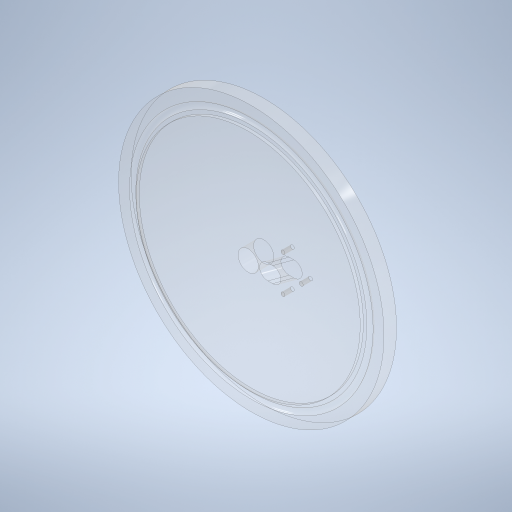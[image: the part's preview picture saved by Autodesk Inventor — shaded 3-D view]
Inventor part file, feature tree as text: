
AUTODESK INVENTOR PART (.ipt)
format: ipt  version: 2023.1 (Build 271208000, 208)  size: 331,264 bytes
history: native  units: mm
features: sketch x7, extrude x4, plane x1, hole x1, revolve x1, other x1
ambient origin geometry x8: Origin, YZ Plane, XZ Plane, XY Plane, X Axis, Y Axis, Z Axis, Center Point
bodies: Solid1 (feature_tree)
feature tree (15):
  extrude  "Extrusion1"  Depth=8.0mm TaperAngle=0.0deg
  extrude  "Extrusion2"  Depth=2.0mm TaperAngle=0.0deg
  extrude  "Extrusion3"  TaperAngle=0.0deg  [1 undecoded]
  sketch  "Sketch4"  dims[d9=45.0mm d10=3.490659mm]
  plane  "Work Plane1"
  extrude  "Extrusion4"  Depth=3.490659mm
  hole  "Hole1"  [1 undecoded]
  revolve  "Revolution1"  [1 undecoded]
  sketch  "Sketch1"  dims[d0=170.0mm d1=8.0mm d2=0.0mm]
  sketch  "Sketch2"  dims[d3=143.5mm d4=2.0mm d5=0.0mm]
  sketch  "Sketch3"  dims[d6=13.0mm d7=0.0mm d8=0.0mm]
  other  "Work Point1"
  sketch  "Sketch5"  dims[d12=10.0mm d13=2.819078mm]
  sketch  "Sketch10"  dims[d14=0.0mm d15=0.0mm d37=2.0mm]
  sketch  "Sketch12"  dims[d50=30.0mm d53=2.459mm d54=6.0mm d55=4.0mm d56=2.0mm d57=90.0deg d58=6.0mm d59=20.594885mm d60=11.65mm d61=1.0mm d63=4.0mm d64=76.0mm d65=90.0deg]
note: 3 required parameter values undecoded (feature->parameter linkage not recoverable at this tier; creation-order binding heuristic only, values carry confidence <= 0.55)